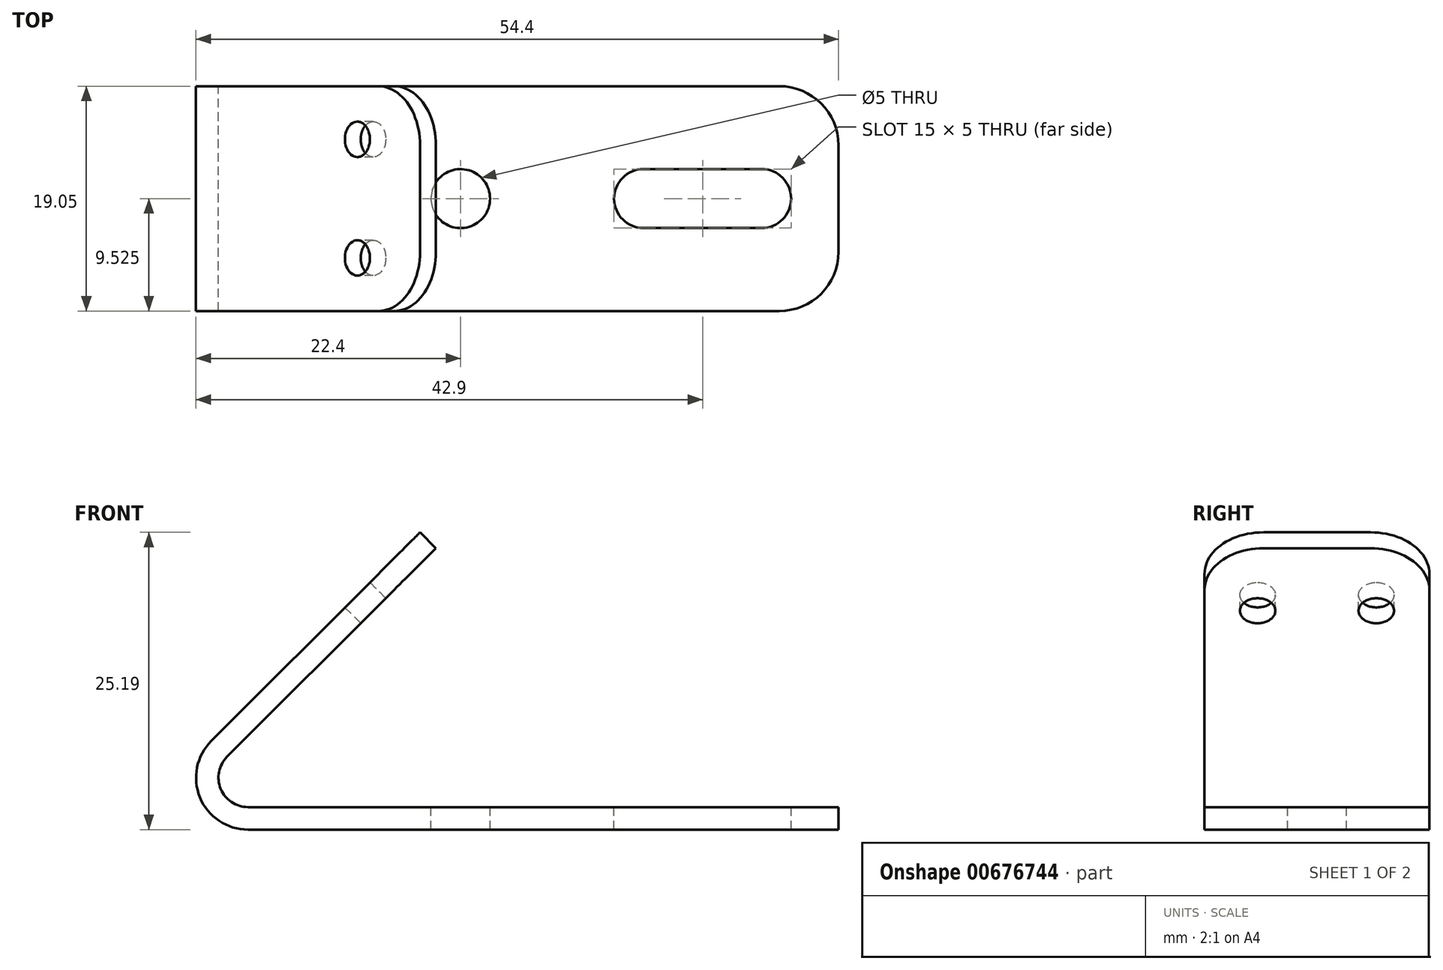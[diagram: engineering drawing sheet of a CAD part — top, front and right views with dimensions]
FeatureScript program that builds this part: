
annotation { "Feature Type Name" : "Feature", "Feature Type Description" : "" }
export const myFeature = defineFeature(function(context is Context, id is Id, definition is map)
    precondition{}
    {
        {
            var Q0;
            Q0=qCreatedBy(makeId("Front.planeOp"),FACE);
            var sketch = newSketch(context, id + "F0", { "sketchPlane" : qUnion([Q0])});
            skArc(sketch, "E0", {"start": v(-53.11, 7.51) * mm, "mid": v(-54.07, 2.72) * mm, "end": v(-50, 0) * mm});
            skLineSegment(sketch, "E1", {"start": v(-53.11, 7.51) * mm, "end": v(-35.43, 25.19) * mm});
            skLineSegment(sketch, "E2", {"start": v(-50, 0) * mm, "end": v(0, 0) * mm});
            skLineSegment(sketch, "E3", {"start": v(-35.43, 25.19) * mm, "end": v(-34.1, 23.85) * mm});
            skArc(sketch, "E4", {"start": v(-51.77, 6.17) * mm, "mid": v(-52.3, 3.44) * mm, "end": v(-50, 1.9) * mm});
            skLineSegment(sketch, "E5", {"start": v(-34.1, 23.85) * mm, "end": v(-51.77, 6.17) * mm});
            skLineSegment(sketch, "E6", {"start": v(0, 0) * mm, "end": v(0, 1.9) * mm});
            skLineSegment(sketch, "E7", {"start": v(0, 1.9) * mm, "end": v(-50, 1.9) * mm});
            skSolve(sketch);
        }
        {
            var Q0;
            Q0=makeQuery(id+"F0.imprint","IMPRINT",FACE,{"disambiguationData":[TD([[makeQuery(id+"F0.imprint","IMPRINT",EDGE,{"derivedFrom":sQuery(id+"F0.wireOp",EDGE,"E0")}),1.0]])]});
            extrude(context, id + "F1", {"entities" : qUnion([Q0]), "depth" : 19.05 * mm, "offsetDistance" : 25 * mm});
        }
        {
            var Q0;
            Q0=makeQuery(id+"F1.opExtrude","SWEPT_FACE",FACE,{"disambiguationData":[OSD([sQuery(id+"F0.wireOp",EDGE,"E7")])]});
            var sketch = newSketch(context, id + "F2", { "sketchPlane" : qUnion([Q0])});
            skCircle(sketch, "E8", {"center": v(-32, -9.53) * mm, "radius": 2.5 * mm});
            skPoint(sketch, "E8.centerSnap0", {"position": v(0, -9.53) * mm});
            skLineSegment(sketch, "E9", {"start": v(0, -9.53) * mm, "end": v(-32, -9.53) * mm, "construction": true});
            skLineSegment(sketch, "E10.bottom", {"start": v(-6.5, -12.03) * mm, "end": v(-16.5, -12.03) * mm});
            skLineSegment(sketch, "E10.top", {"start": v(-6.5, -7.03) * mm, "end": v(-16.5, -7.03) * mm});
            skPoint(sketch, "E10.middle", {"position": v(-11.5, -9.53) * mm});
            skArc(sketch, "E11", {"start": v(-16.5, -7.03) * mm, "mid": v(-19, -9.53) * mm, "end": v(-16.5, -12.03) * mm});
            skArc(sketch, "E12", {"start": v(-6.5, -12.03) * mm, "mid": v(-4, -9.53) * mm, "end": v(-6.5, -7.03) * mm});
            skSolve(sketch);
        }
        {
            var Q0;
            Q0=makeQuery(id+"F2.imprint","IMPRINT",FACE,{"disambiguationData":[TD([[makeQuery(id+"F2.imprint","IMPRINT",EDGE,{"derivedFrom":sQuery(id+"F2.wireOp",EDGE,"E8")}),1.0]])]});
            var Q1;
            Q1=makeQuery(id+"F2.imprint","IMPRINT",FACE,{"disambiguationData":[TD([[makeQuery(id+"F2.imprint","IMPRINT",EDGE,{"derivedFrom":sQuery(id+"F2.wireOp",EDGE,"E10.bottom")}),-1.0]])]});
            extrude(context, id + "F3", {"entities" : qUnion([Q0, Q1]), "operationType" : NewBodyOperationType.REMOVE, "oppositeDirection" : true, "depth" : 25 * mm, "offsetDistance" : 25 * mm});
        }
        {
            var Q0;
            Q0=makeQuery(id+"F1.opExtrude","SWEPT_FACE",FACE,{"disambiguationData":[OSD([sQuery(id+"F0.wireOp",EDGE,"E1")])]});
            var sketch = newSketch(context, id + "F4", { "sketchPlane" : qUnion([Q0])});
            skCircle(sketch, "E13", {"center": v(4.5, -14.74) * mm, "radius": 1.5 * mm});
            skCircle(sketch, "E14", {"center": v(14.55, -14.74) * mm, "radius": 1.5 * mm});
            skSolve(sketch);
        }
        {
            var Q0;
            Q0=makeQuery(id+"F4.imprint","IMPRINT",FACE,{"disambiguationData":[TD([[makeQuery(id+"F4.imprint","IMPRINT",EDGE,{"derivedFrom":sQuery(id+"F4.wireOp",EDGE,"E14")}),1.0]])]});
            var Q1;
            Q1=makeQuery(id+"F4.imprint","IMPRINT",FACE,{"disambiguationData":[TD([[makeQuery(id+"F4.imprint","IMPRINT",EDGE,{"derivedFrom":sQuery(id+"F4.wireOp",EDGE,"E13")}),1.0]])]});
            var Q2;
            Q2=sQuery(id+"F4.wireOp",EDGE,"E13");
            var Q3;
            Q3=sQuery(id+"F4.wireOp",EDGE,"E14");
            extrude(context, id + "F5", {"entities" : qUnion([Q0, Q1]), "operationType" : NewBodyOperationType.REMOVE, "surfaceEntities" : qUnion([Q2, Q3]), "oppositeDirection" : true, "depth" : 7 * mm, "offsetDistance" : 25 * mm});
        }
        {
            var Q0;
            Q0=makeQuery(id+"F1.opExtrude","CAP_EDGE",EDGE,{"disambiguationData":[OSD([sQuery(id+"F0.wireOp",EDGE,"E6")])],"isStart":false});
            var Q1;
            Q1=makeQuery(id+"F1.opExtrude","CAP_EDGE",EDGE,{"disambiguationData":[OSD([sQuery(id+"F0.wireOp",EDGE,"E6")])],"isStart":true});
            var Q2;
            Q2=makeQuery(id+"F1.opExtrude","CAP_EDGE",EDGE,{"disambiguationData":[OSD([sQuery(id+"F0.wireOp",EDGE,"E3")])],"isStart":false});
            var Q3;
            Q3=makeQuery(id+"F1.opExtrude","CAP_EDGE",EDGE,{"disambiguationData":[OSD([sQuery(id+"F0.wireOp",EDGE,"E3")])],"isStart":true});
            fillet(context, id + "F6", {"entities" : qUnion([Q0, Q1, Q2, Q3]), "radius" : 5 * mm, "tangentPropagation" : true, "allowEdgeOverflow" : false});
        }
    });
